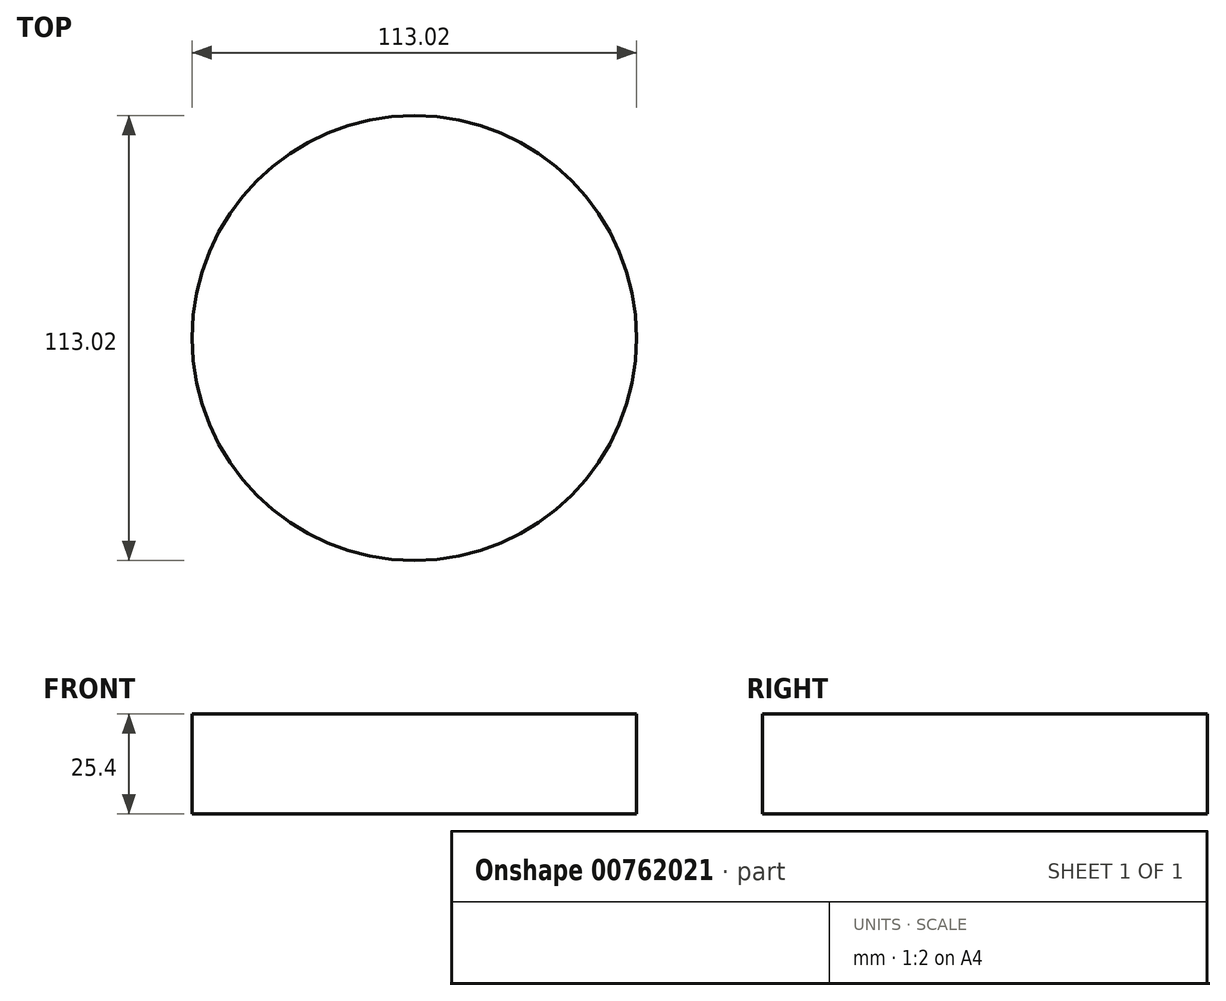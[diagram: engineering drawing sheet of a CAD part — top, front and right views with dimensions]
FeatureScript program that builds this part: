
annotation { "Feature Type Name" : "Feature", "Feature Type Description" : "" }
export const myFeature = defineFeature(function(context is Context, id is Id, definition is map)
    precondition{}
    {
        {
            var Q0;
            Q0=qCreatedBy(makeId("Top.planeOp"),FACE);
            var sketch = newSketch(context, id + "F0", { "sketchPlane" : qUnion([Q0])});
            skCircle(sketch, "E0", {"center": v(0, 0) * mm, "radius": 56.5 * mm});
            skSolve(sketch);
        }
        {
            var Q0;
            Q0=makeQuery(id+"F0.imprint","IMPRINT",FACE,{"disambiguationData":[TD([[makeQuery(id+"F0.imprint","IMPRINT",EDGE,{"derivedFrom":sQuery(id+"F0.wireOp",EDGE,"E0")}),1.0]])]});
            extrude(context, id + "F1", {"entities" : qUnion([Q0]), "depth" : 25.4 * mm, "offsetDistance" : 25.4 * mm});
        }
    });
